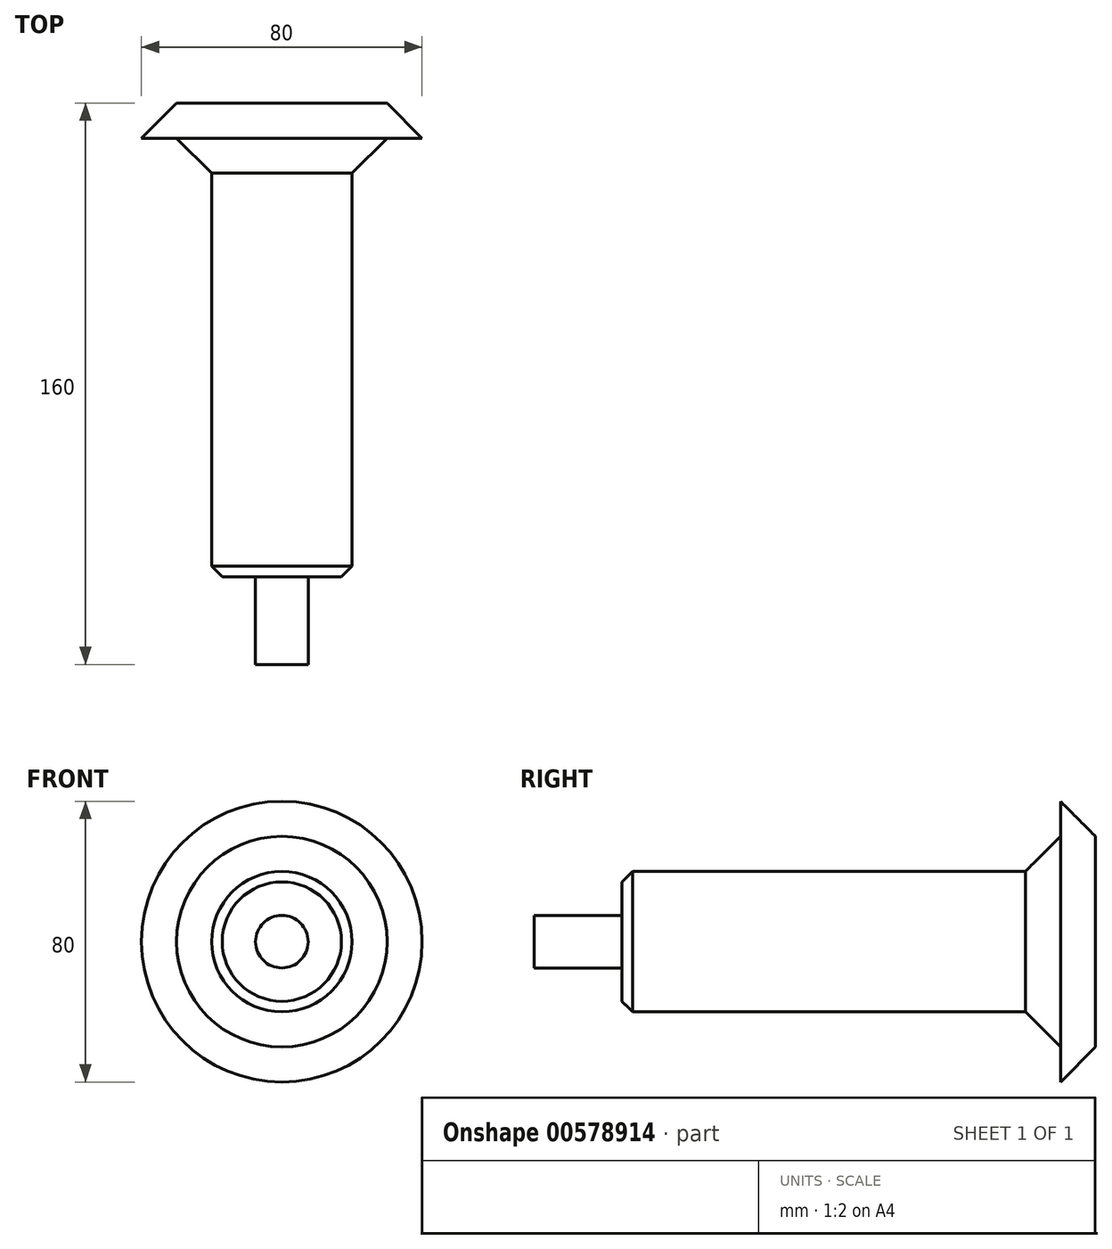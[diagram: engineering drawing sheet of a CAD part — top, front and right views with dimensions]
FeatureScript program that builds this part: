
annotation { "Feature Type Name" : "Feature", "Feature Type Description" : "" }
export const myFeature = defineFeature(function(context is Context, id is Id, definition is map)
    precondition{}
    {
        {
            var Q0;
            Q0=qCreatedBy(makeId("Front.planeOp"),FACE);
            var sketch = newSketch(context, id + "F0", { "sketchPlane" : qUnion([Q0])});
            skCircle(sketch, "E0", {"center": v(0, 0) * mm, "radius": 20 * mm});
            skSolve(sketch);
        }
        {
            var Q0;
            Q0 = qSketchRegion(id + "F0", true);
            extrude(context, id + "F1", {"entities" : qUnion([Q0]), "depth" : (150 - 35) * mm, "offsetDistance" : 25 * mm});
        }
        {
            var Q0;
            Q0=makeQuery(id+"F1.opExtrude","CAP_EDGE",EDGE,{"disambiguationData":[OSD([sQuery(id+"F0.wireOp",EDGE,"E0")])],"isStart":false});
            chamfer(context, id + "F2", {"entities" : qUnion([Q0]), "width" : 3 * mm, "tangentPropagation" : true});
        }
        {
            var Q0;
            Q0=makeQuery(id+"F1.opExtrude","CAP_FACE",FACE,{"disambiguationData":[OSD([sQuery(id+"F0.wireOp",EDGE,"E0")])],"isStart":false});
            var sketch = newSketch(context, id + "F3", { "sketchPlane" : qUnion([Q0])});
            skCircle(sketch, "E1", {"center": v(0, 0) * mm, "radius": 7.5 * mm});
            skSolve(sketch);
        }
        {
            var Q0;
            Q0 = qSketchRegion(id + "F3", true);
            extrude(context, id + "F4", {"entities" : qUnion([Q0]), "operationType" : NewBodyOperationType.ADD, "depth" : 25 * mm, "offsetDistance" : 25 * mm});
        }
        {
            var Q0;
            Q0=makeQuery(id+"F1.opExtrude","CAP_FACE",FACE,{"disambiguationData":[OSD([sQuery(id+"F0.wireOp",EDGE,"E0")])],"isStart":true});
            var sketch = newSketch(context, id + "F5", { "sketchPlane" : qUnion([Q0])});
            skCircle(sketch, "E2", {"center": v(0, 0) * mm, "radius": 30 * mm});
            skSolve(sketch);
        }
        {
            var Q0;
            Q0 = qSketchRegion(id + "F5", true);
            extrude(context, id + "F6", {"entities" : qUnion([Q0]), "operationType" : NewBodyOperationType.ADD, "depth" : 10 * mm, "offsetDistance" : 25 * mm});
        }
        {
            var Q0;
            Q0=makeQuery(id+"F6.opExtrude","CAP_FACE",FACE,{"disambiguationData":[OSD([sQuery(id+"F5.wireOp",EDGE,"E2")])],"isStart":false});
            var sketch = newSketch(context, id + "F7", { "sketchPlane" : qUnion([Q0])});
            skCircle(sketch, "E3", {"center": v(0, 0) * mm, "radius": 40 * mm});
            skSolve(sketch);
        }
        {
            var Q0;
            Q0 = qSketchRegion(id + "F7", true);
            extrude(context, id + "F8", {"entities" : qUnion([Q0]), "operationType" : NewBodyOperationType.ADD, "depth" : 10 * mm, "offsetDistance" : 25 * mm});
        }
        {
            var Q0;
            Q0=makeQuery(id+"F8.opExtrude","CAP_EDGE",EDGE,{"disambiguationData":[OSD([sQuery(id+"F7.wireOp",EDGE,"E3")])],"isStart":false});
            var Q1;
            Q1=makeQuery(id+"F6.opExtrude","CAP_EDGE",EDGE,{"disambiguationData":[OSD([sQuery(id+"F5.wireOp",EDGE,"E2")])],"isStart":true});
            chamfer(context, id + "F9", {"entities" : qUnion([Q0, Q1]), "width" : 10 * mm, "tangentPropagation" : true});
        }
    });
